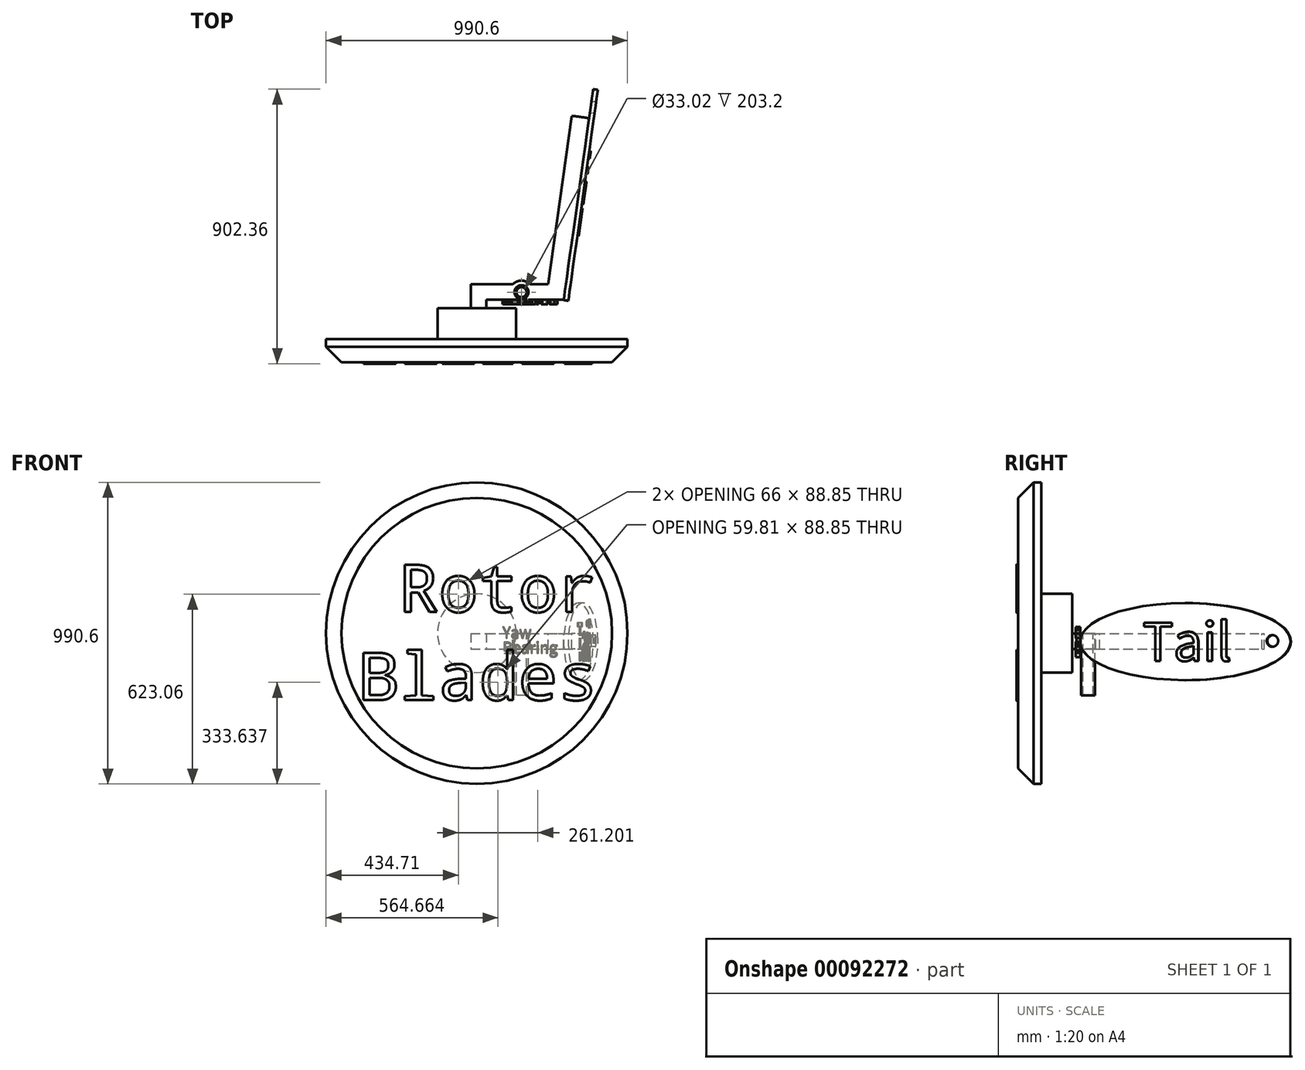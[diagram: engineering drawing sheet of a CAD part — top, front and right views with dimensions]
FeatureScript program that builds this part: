
annotation { "Feature Type Name" : "Feature", "Feature Type Description" : "" }
export const myFeature = defineFeature(function(context is Context, id is Id, definition is map)
    precondition{}
    {
        {
            var Q0;
            Q0=qCreatedBy(makeId("Front.planeOp"),FACE);
            cPlane(context, id + "F0", {"entities" : qUnion([Q0]), "cplaneType" : CPlaneType.OFFSET, "offset" : 50.8 * mm, "width" : 152.4 * mm, "height" : 152.4 * mm});
        }
        {
            var Q0;
            Q0=qCreatedBy(id+"F0.planeOp",FACE);
            var sketch = newSketch(context, id + "F1", { "sketchPlane" : qUnion([Q0])});
            skCircle(sketch, "E0", {"center": v(0.15, 50.7) * mm, "radius": 495.3 * mm});
            skSolve(sketch);
        }
        {
            var Q0;
            Q0=makeQuery(id+"F1.imprint","IMPRINT",FACE,{"disambiguationData":[TD([[makeQuery(id+"F1.imprint","IMPRINT",EDGE,{"derivedFrom":sQuery(id+"F1.wireOp",EDGE,"E0")}),1.0]])]});
            extrude(context, id + "F2", {"entities" : qUnion([Q0]), "depth" : 76.2 * mm});
        }
        {
            var Q0;
            Q0=makeQuery(id+"F2.opExtrude","CAP_EDGE",EDGE,{"disambiguationData":[OSD([sQuery(id+"F1.wireOp",EDGE,"E0")])],"isStart":false});
            chamfer(context, id + "F3", {"entities" : qUnion([Q0]), "width" : 50.8 * mm, "tangentPropagation" : true});
        }
        {
            var Q0;
            Q0=makeQuery(id+"F2.opExtrude","CAP_FACE",FACE,{"disambiguationData":[OSD([sQuery(id+"F1.wireOp",EDGE,"E0")])],"isStart":false});
            var sketch = newSketch(context, id + "F4", { "sketchPlane" : qUnion([Q0])});
            skText(sketch, "E1", { "text": " Rotor \nBlades", "fontName": "DroidSansMono.ttf"});
            const initialGuessF4  = {"E1": [-0.38684, 0.12014, 1, 0, 0.15668]};
            skSetInitialGuess(sketch, initialGuessF4);
            skSolve(sketch);
        }
        {
            var Q0;
            Q0 = qSketchRegion(id + "F4", true);
            extrude(context, id + "F5", {"entities" : qUnion([Q0]), "depth" : 5.08 * mm});
        }
        {
            var Q0;
            Q0=qCreatedBy(makeId("Top.planeOp"),FACE);
            cPlane(context, id + "F6", {"entities" : qUnion([Q0]), "cplaneType" : CPlaneType.OFFSET, "offset" : 49.67 * mm, "width" : 152.4 * mm, "height" : 152.4 * mm});
        }
        {
            var Q0;
            Q0=qCreatedBy(id+"F6.planeOp",FACE);
            var sketch = newSketch(context, id + "F7", { "sketchPlane" : qUnion([Q0])});
            skLineSegment(sketch, "E2.top", {"start": v(-19.27, 128.84) * mm, "end": v(118.77, 128.84) * mm});
            skLineSegment(sketch, "E2.left", {"start": v(-19.27, -74.36) * mm, "end": v(-19.27, 128.84) * mm});
            skLineSegment(sketch, "E3.0", {"start": v(31.53, -74.36) * mm, "end": v(31.53, 78.04) * mm});
            skArc(sketch, "E4", {"start": v(-19.27, -74.36) * mm, "mid": v(6.13, -99.76) * mm, "end": v(31.53, -74.36) * mm});
            skLineSegment(sketch, "E5.0", {"start": v(31.53, 78.04) * mm, "end": v(118.26, 78.04) * mm});
            skCircle(sketch, "E6", {"center": v(146.9, 103.15) * mm, "radius": 22.86 * mm});
            skLineSegment(sketch, "E7", {"start": v(234.73, 128.84) * mm, "end": v(312.5, 682.2) * mm});
            skLineSegment(sketch, "E8.0", {"start": v(285.53, 78.04) * mm, "end": v(369.32, 674.21) * mm});
            skArc(sketch, "E9", {"start": v(369.32, 674.21) * mm, "mid": v(341, 678.9) * mm, "end": v(312.5, 682.2) * mm});
            skArc(sketch, "E10", {"start": v(175.05, 128.84) * mm, "mid": v(146.9, 141.25) * mm, "end": v(118.77, 128.84) * mm});
            skLineSegment(sketch, "E11.trimOffspring", {"start": v(175.05, 128.84) * mm, "end": v(234.73, 128.84) * mm});
            skLineSegment(sketch, "E12.trimOffspring", {"start": v(175.56, 78.04) * mm, "end": v(285.53, 78.04) * mm});
            skArc(sketch, "E13.trimOffspring", {"start": v(118.26, 78.04) * mm, "mid": v(146.9, 65.05) * mm, "end": v(175.56, 78.04) * mm});
            skSolve(sketch);
        }
        {
            var Q0;
            Q0=makeQuery(id+"F7.imprint","IMPRINT",FACE,{"disambiguationData":[TD([[makeQuery(id+"F7.imprint","IMPRINT",EDGE,{"derivedFrom":sQuery(id+"F7.wireOp",EDGE,"E2.top")}),-1.0]])]});
            extrude(context, id + "F8", {"entities" : qUnion([Q0]), "oppositeDirection" : true, "depth" : 50.8 * mm});
        }
        {
            var Q0;
            Q0=makeQuery(id+"F8.opExtrude","SWEPT_FACE",FACE,{"disambiguationData":[OSD([sQuery(id+"F7.wireOp",EDGE,"E5.0")])]});
            cPlane(context, id + "F9", {"entities" : qUnion([Q0]), "cplaneType" : CPlaneType.OFFSET, "offset" : 0 * mm, "width" : 152.4 * mm, "height" : 152.4 * mm});
        }
        {
            var Q0;
            Q0=qCreatedBy(id+"F9.planeOp",FACE);
            var sketch = newSketch(context, id + "F10", { "sketchPlane" : qUnion([Q0])});
            skText(sketch, "E14", { "text": "Yaw\nBearing", "fontName": "NotoSansCJKjp-Regular.otf"});
            const initialGuessF10  = {"E14": [0.08472, 0.03436, 1, 0, 0.03605]};
            skSetInitialGuess(sketch, initialGuessF10);
            skSolve(sketch);
        }
        {
            var Q0;
            Q0 = qSketchRegion(id + "F10", true);
            extrude(context, id + "F11", {"entities" : qUnion([Q0]), "depth" : 15.24 * mm});
        }
        {
            var Q0;
            Q0=makeQuery(id+"F8.opExtrude","SWEPT_FACE",FACE,{"disambiguationData":[OSD([sQuery(id+"F7.wireOp",EDGE,"E8.0")])]});
            cPlane(context, id + "F12", {"entities" : qUnion([Q0]), "cplaneType" : CPlaneType.OFFSET, "offset" : 0 * mm, "width" : 152.4 * mm, "height" : 152.4 * mm});
        }
        {
            var Q0;
            Q0=qCreatedBy(id+"F12.planeOp",FACE);
            var sketch = newSketch(context, id + "F13", { "sketchPlane" : qUnion([Q0])});
            skEllipse(sketch, "E15", {"center": v(466.02, 22.8) * mm, "majorRadius": 350.05 * mm, "minorRadius": 127 * mm, "majorAxis": v(1, 0)});
            skCircle(sketch, "E16", {"center": v(756.38, 25) * mm, "radius": 19.05 * mm});
            skSolve(sketch);
        }
        {
            var Q0;
            Q0=makeQuery(id+"F13.imprint","IMPRINT",FACE,{"disambiguationData":[TD([[makeQuery(id+"F13.imprint","IMPRINT",EDGE,{"derivedFrom":sQuery(id+"F13.wireOp",EDGE,"E15")}),1.0]])]});
            extrude(context, id + "F14", {"entities" : qUnion([Q0]), "depth" : 15.24 * mm});
        }
        {
            var Q0;
            Q0=makeQuery(id+"F14.opExtrude","CAP_FACE",FACE,{"disambiguationData":[OSD([sQuery(id+"F13.wireOp",EDGE,"E15"),sQuery(id+"F13.wireOp",EDGE,"E16")])],"isStart":false});
            var sketch = newSketch(context, id + "F15", { "sketchPlane" : qUnion([Q0])});
            skText(sketch, "E17", { "text": "Tail", "fontName": "NotoSansCJKjp-Regular.otf"});
            const initialGuessF15  = {"E17": [0.3255, -0.04036, 1, 0, 0.12354]};
            skSetInitialGuess(sketch, initialGuessF15);
            skSolve(sketch);
        }
        {
            var Q0;
            Q0 = qSketchRegion(id + "F15", true);
            extrude(context, id + "F16", {"entities" : qUnion([Q0]), "operationType" : NewBodyOperationType.ADD, "depth" : 5.08 * mm});
        }
        {
            var Q0;
            Q0=makeQuery(id+"F7.imprint","IMPRINT",FACE,{"disambiguationData":[TD([[makeQuery(id+"F7.imprint","IMPRINT",EDGE,{"derivedFrom":sQuery(id+"F7.wireOp",EDGE,"E2.top")}),-1.0]])]});
            var sketch = newSketch(context, id + "F17", { "sketchPlane" : qUnion([Q0])});
            skCircle(sketch, "E18.0", {"center": v(146.9, 103.15) * mm, "radius": 22.86 * mm});
            skCircle(sketch, "E19.0", {"center": v(146.9, 103.15) * mm, "radius": 16.51 * mm});
            skSolve(sketch);
        }
        {
            var Q0;
            Q0 = qSketchRegion(id + "F17", true);
            extrude(context, id + "F18", {"entities" : qUnion([Q0]), "oppositeDirection" : true, "depth" : 203.2 * mm});
        }
        {
            var Q0;
            Q0=makeQuery(id+"F1.imprint","IMPRINT",FACE,{"disambiguationData":[TD([[makeQuery(id+"F1.imprint","IMPRINT",EDGE,{"derivedFrom":sQuery(id+"F1.wireOp",EDGE,"E0")}),1.0]])]});
            var sketch = newSketch(context, id + "F19", { "sketchPlane" : qUnion([Q0])});
            skCircle(sketch, "E20.0", {"center": v(0.15, 50.7) * mm, "radius": 129.05 * mm});
            skSolve(sketch);
        }
        {
            var Q0;
            Q0 = qSketchRegion(id + "F19", true);
            extrude(context, id + "F20", {"entities" : qUnion([Q0]), "operationType" : NewBodyOperationType.ADD, "oppositeDirection" : true, "depth" : 101.6 * mm});
        }
    });
